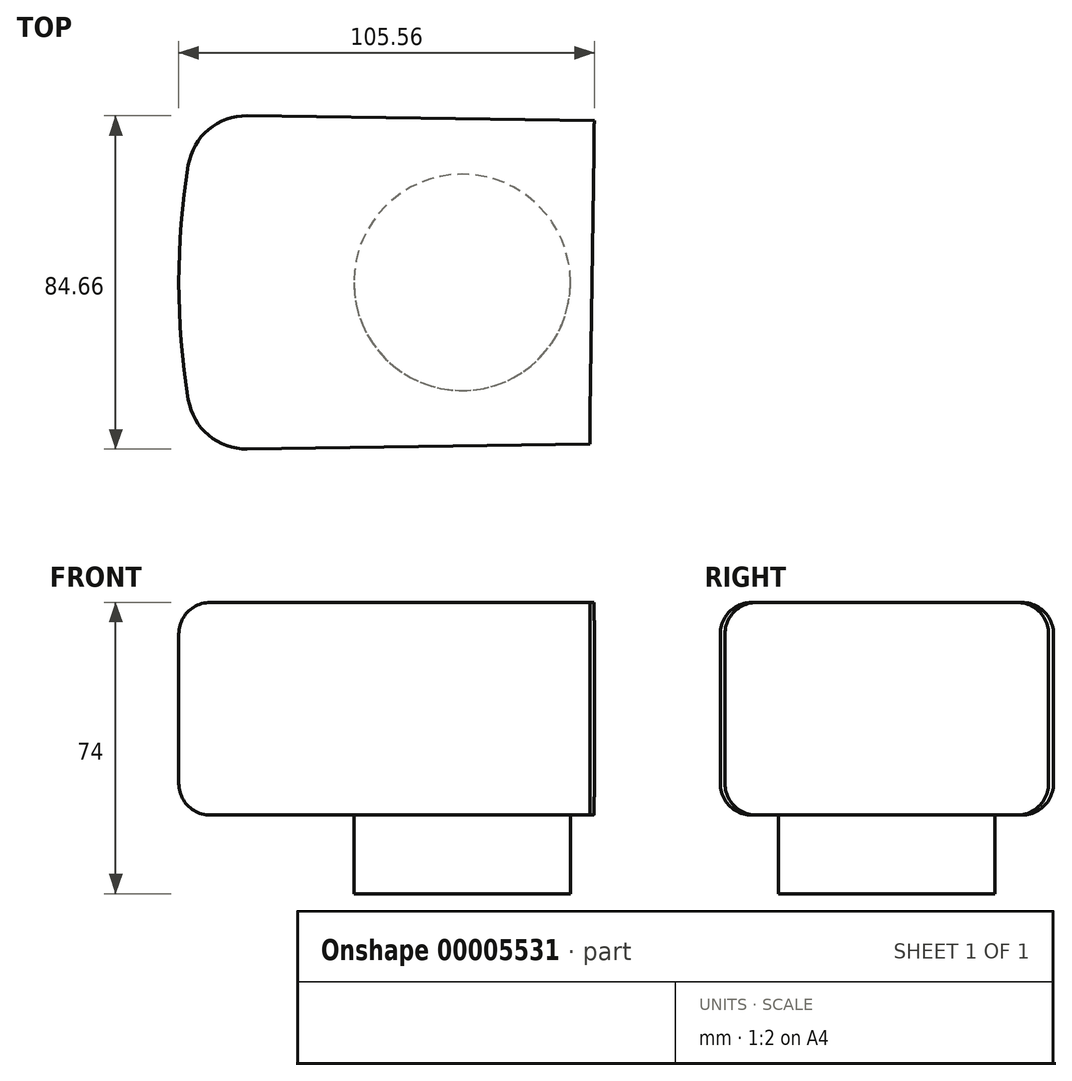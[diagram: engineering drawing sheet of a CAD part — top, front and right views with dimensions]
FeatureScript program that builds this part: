
annotation { "Feature Type Name" : "Feature", "Feature Type Description" : "" }
export const myFeature = defineFeature(function(context is Context, id is Id, definition is map)
    precondition{}
    {
        {
            var Q0;
            Q0=qCreatedBy(makeId("Top.planeOp"),FACE);
            var sketch = newSketch(context, id + "F0", { "sketchPlane" : qUnion([Q0])});
            skArc(sketch, "E0", {"start": v(-180.05, 42.5) * mm, "mid": v(-185, 0) * mm, "end": v(-180.05, -42.5) * mm});
            skLineSegment(sketch, "E1", {"start": v(-180.05, 42.5) * mm, "end": v(-79.44, 41.1) * mm});
            skLineSegment(sketch, "E2", {"start": v(-80.58, -41.12) * mm, "end": v(-180.05, -42.5) * mm});
            skLineSegment(sketch, "E3", {"start": v(-79.44, 41.1) * mm, "end": v(-80.58, -41.12) * mm});
            skPoint(sketch, "E4.end.orphan", {"position": v(0, 40) * mm});
            skPoint(sketch, "E5.orphan", {"position": v(0, -40) * mm});
            skSolve(sketch);
        }
        {
            var Q0;
            Q0=makeQuery(id+"F0.imprint","IMPRINT",FACE,{"disambiguationData":[TD([[makeQuery(id+"F0.imprint","IMPRINT",EDGE,{"derivedFrom":sQuery(id+"F0.wireOp",EDGE,"E0")}),1.0]])]});
            extrude(context, id + "F1", {"entities" : qUnion([Q0]), "depth" : 54 * mm});
        }
        {
            var Q0;
            Q0=makeQuery(id+"F1.opExtrude","SWEPT_EDGE",EDGE,{"disambiguationData":[OSD([sQuery(id+"F0.wireOp",EDGE,"E0"),sQuery(id+"F0.wireOp",EDGE,"E2")])]});
            var Q1;
            Q1=makeQuery(id+"F1.opExtrude","SWEPT_EDGE",EDGE,{"disambiguationData":[OSD([sQuery(id+"F0.wireOp",EDGE,"E0"),sQuery(id+"F0.wireOp",EDGE,"E1")])]});
            fillet(context, id + "F2", {"entities" : qUnion([Q0, Q1]), "radius" : 15 * mm, "tangentPropagation" : true, "allowEdgeOverflow" : false});
        }
        {
            var Q0;
            Q0=makeQuery(id+"F1.opExtrude","CAP_FACE",FACE,{"disambiguationData":[OSD([sQuery(id+"F0.wireOp",EDGE,"E0"),sQuery(id+"F0.wireOp",EDGE,"E1"),sQuery(id+"F0.wireOp",EDGE,"E2"),sQuery(id+"F0.wireOp",EDGE,"E3")])],"isStart":true});
            var sketch = newSketch(context, id + "F3", { "sketchPlane" : qUnion([Q0])});
            skLineSegment(sketch, "E6", {"start": v(-74.44, 41.03) * mm, "end": v(-43, 0) * mm});
            skLineSegment(sketch, "E7", {"start": v(-43, 0) * mm, "end": v(-74.44, -41.03) * mm});
            skLineSegment(sketch, "E8", {"start": v(-74.44, 41.03) * mm, "end": v(47.2, 55.89) * mm});
            skLineSegment(sketch, "E9", {"start": v(47.2, 55.89) * mm, "end": v(48.63, -68.12) * mm});
            skLineSegment(sketch, "E10", {"start": v(48.63, -68.12) * mm, "end": v(-74.44, -41.03) * mm});
            skSolve(sketch);
        }
        {
            var Q0;
            Q0=makeQuery(id+"F3.imprint","IMPRINT",FACE,{"disambiguationData":[TD([[makeQuery(id+"F3.imprint","IMPRINT",EDGE,{"derivedFrom":sQuery(id+"F3.wireOp",EDGE,"E6")}),1.0]])]});
            extrude(context, id + "F4", {"entities" : qUnion([Q0]), "operationType" : NewBodyOperationType.REMOVE, "oppositeDirection" : true, "depth" : 39 * mm});
        }
        {
            var Q0;
            Q0=makeQuery(id+"F1.opExtrude","CAP_EDGE",EDGE,{"disambiguationData":[OSD([sQuery(id+"F0.wireOp",EDGE,"E1")])],"isStart":false});
            var Q1;
            Q1=makeQuery(id+"F1.opExtrude","CAP_EDGE",EDGE,{"disambiguationData":[OSD([sQuery(id+"F0.wireOp",EDGE,"E1")])],"isStart":true});
            fillet(context, id + "F5", {"entities" : qUnion([Q0, Q1]), "radius" : 8 * mm, "tangentPropagation" : true, "allowEdgeOverflow" : false});
        }
        {
            var Q0;
            Q0=makeQuery(id+"F1.opExtrude","CAP_FACE",FACE,{"disambiguationData":[OSD([sQuery(id+"F0.wireOp",EDGE,"E0"),sQuery(id+"F0.wireOp",EDGE,"E1"),sQuery(id+"F0.wireOp",EDGE,"E2"),sQuery(id+"F0.wireOp",EDGE,"E3")])],"isStart":true});
            var sketch = newSketch(context, id + "F6", { "sketchPlane" : qUnion([Q0])});
            skCircle(sketch, "E11", {"center": v(-113, 0) * mm, "radius": 27.5 * mm});
            skSolve(sketch);
        }
        {
            var Q0;
            Q0=makeQuery(id+"F6.imprint","IMPRINT",FACE,{"disambiguationData":[TD([[makeQuery(id+"F6.imprint","IMPRINT",EDGE,{"derivedFrom":sQuery(id+"F6.wireOp",EDGE,"E11")}),1.0]])]});
            extrude(context, id + "F7", {"entities" : qUnion([Q0]), "operationType" : NewBodyOperationType.ADD, "depth" : 20 * mm});
        }
    });
